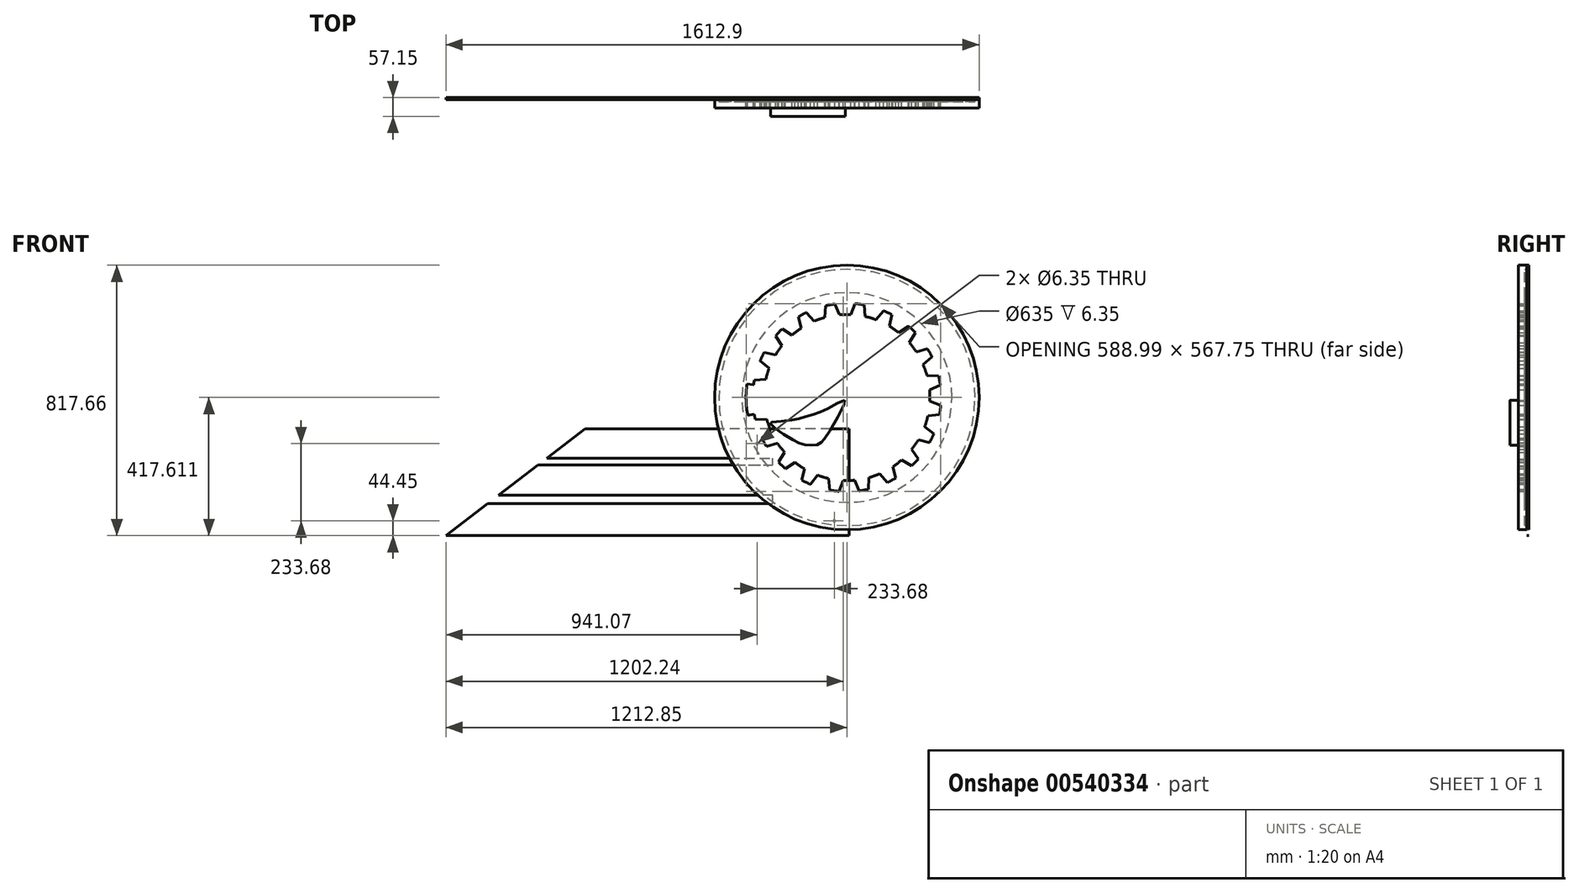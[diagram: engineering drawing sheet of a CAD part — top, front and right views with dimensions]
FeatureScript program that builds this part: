
annotation { "Feature Type Name" : "Feature", "Feature Type Description" : "" }
export const myFeature = defineFeature(function(context is Context, id is Id, definition is map)
    precondition{}
    {
        {
            var Q0;
            Q0=qCreatedBy(makeId("Front.planeOp"),FACE);
            var sketch = newSketch(context, id + "F0", { "sketchPlane" : qUnion([Q0])});
            skLineSegment(sketch, "E0", {"start": v(0, -90.2) * mm, "end": v(0, 1030.2) * mm, "construction": true});
            skLineSegment(sketch, "E1", {"start": v(0, 0) * mm, "end": v(-1219.2, 0) * mm});
            skLineSegment(sketch, "E2", {"start": v(-1219.2, 0) * mm, "end": v(-610.08, 467.36) * mm, "construction": true});
            skLineSegment(sketch, "E3", {"start": v(-1219.2, 0) * mm, "end": v(-1093.4, 96.52) * mm});
            skLineSegment(sketch, "E4", {"start": v(-1093.4, 96.52) * mm, "end": v(-231.3, 96.52) * mm});
            skLineSegment(sketch, "E5", {"start": v(0, 96.52) * mm, "end": v(0, 0) * mm});
            skLineSegment(sketch, "E6", {"start": v(-231.3, 121.92) * mm, "end": v(-1060.3, 121.92) * mm});
            skLineSegment(sketch, "E7", {"start": v(-1060.3, 121.92) * mm, "end": v(-941.12, 213.36) * mm});
            skLineSegment(sketch, "E8", {"start": v(-941.12, 213.36) * mm, "end": v(-231.3, 213.36) * mm});
            skLineSegment(sketch, "E9", {"start": v(0, 213.36) * mm, "end": v(0, 121.92) * mm});
            skLineSegment(sketch, "E10", {"start": v(-914.64, 233.68) * mm, "end": v(-231.3, 233.68) * mm});
            skLineSegment(sketch, "E11", {"start": v(0, 233.68) * mm, "end": v(0, 322.58) * mm});
            skLineSegment(sketch, "E12", {"start": v(0, 322.58) * mm, "end": v(-798.77, 322.58) * mm});
            skLineSegment(sketch, "E13", {"start": v(-798.77, 322.58) * mm, "end": v(-914.64, 233.68) * mm});
            skLineSegment(sketch, "E14", {"start": v(-231.3, 96.52) * mm, "end": v(-231.3, 121.92) * mm});
            skLineSegment(sketch, "E15", {"start": v(-231.3, 322.58) * mm, "end": v(0, 322.58) * mm});
            skLineSegment(sketch, "E16.trimOffspring", {"start": v(-231.3, 213.36) * mm, "end": v(-231.3, 233.68) * mm});
            skLineSegment(sketch, "E17", {"start": v(0, 322.58) * mm, "end": v(0, 0) * mm});
            skLineSegment(sketch, "E18", {"start": v(-322.58, 322.58) * mm, "end": v(-322.58, 0) * mm, "construction": true});
            skLineSegment(sketch, "E19", {"start": v(-322.58, 322.58) * mm, "end": v(0, 0) * mm, "construction": true});
            skLineSegment(sketch, "E20", {"start": v(0, 278.13) * mm, "end": v(-322.58, 278.13) * mm, "construction": true});
            skPoint(sketch, "E21.start.orphan", {"position": v(0, 48.26) * mm});
            skLineSegment(sketch, "E22.0", {"start": v(0, 44.45) * mm, "end": v(-1219.2, 44.45) * mm, "construction": true});
            skCircle(sketch, "E23", {"center": v(-278.13, 278.13) * mm, "radius": 3.18 * mm});
            skCircle(sketch, "E24", {"center": v(-44.45, 44.45) * mm, "radius": 3.18 * mm});
            skSolve(sketch);
        }
        {
            var Q0;
            {var subQ0=sQuery(id+"F0.wireOp",EDGE,"E1");Q0=makeQuery(id+"F0.imprint","IMPRINT",FACE,{"disambiguationData":[TD([[makeQuery(id+"F0.imprint","IMPRINT",EDGE,{"derivedFrom":subQ0}),-1.0]])]});}
            extrude(context, id + "F1", {"entities" : qUnion([Q0]), "depth" : 6.35 * mm, "offsetDistance" : 25.4 * mm});
        }
        {
            var Q0;
            Q0=qCreatedBy(makeId("Front.planeOp"),FACE);
            var sketch = newSketch(context, id + "F2", { "sketchPlane" : qUnion([Q0])});
            skCircle(sketch, "E25", {"center": v(-6.35, 417.61) * mm, "radius": 400.05 * mm});
            skSolve(sketch);
        }
        {
            var Q0;
            Q0 = qSketchRegion(id + "F2", true);
            extrude(context, id + "F3", {"entities" : qUnion([Q0]), "depth" : 6.35 * mm, "offsetDistance" : 25.4 * mm});
        }
        {
            var Q0;
            Q0=makeQuery(id+"F3.opExtrude","CAP_FACE",FACE,{"disambiguationData":[OSD([sQuery(id+"F2.wireOp",EDGE,"E25")])],"isStart":false});
            var sketch = newSketch(context, id + "F4", { "sketchPlane" : qUnion([Q0])});
            skCircle(sketch, "E26.0", {"center": v(-6.35, 417.61) * mm, "radius": 400.05 * mm});
            skCircle(sketch, "E27", {"center": v(-6.35, 417.61) * mm, "radius": 387.35 * mm});
            skCircle(sketch, "E28", {"center": v(-6.35, 417.61) * mm, "radius": 317.5 * mm});
            skSolve(sketch);
        }
        {
            var Q0;
            Q0=makeQuery(id+"F4.imprint","IMPRINT",FACE,{"disambiguationData":[TD([[makeQuery(id+"F4.imprint","IMPRINT",EDGE,{"derivedFrom":sQuery(id+"F4.wireOp",EDGE,"E27")}),1.0]])]});
            extrude(context, id + "F5", {"entities" : qUnion([Q0]), "depth" : 6.35 * mm, "offsetDistance" : 25.4 * mm});
        }
        {
            var Q0;
            Q0=makeQuery(id+"F3.opExtrude","CAP_FACE",FACE,{"disambiguationData":[OSD([sQuery(id+"F2.wireOp",EDGE,"E25")])],"isStart":false});
            var sketch = newSketch(context, id + "F6", { "sketchPlane" : qUnion([Q0])});
            skCircle(sketch, "E29.0", {"center": v(-6.35, 417.61) * mm, "radius": 400.05 * mm});
            skArc(sketch, "E30", {"start": v(-306.57, 363) * mm, "mid": v(-309.93, 386.72) * mm, "end": v(-311.42, 410.64) * mm});
            skArc(sketch, "E31", {"start": v(-286.62, 366.63) * mm, "mid": v(-287.82, 373.7) * mm, "end": v(-288.84, 380.81) * mm});
            skArc(sketch, "E32", {"start": v(-256.45, 394.63) * mm, "mid": v(-257.1, 403.24) * mm, "end": v(-257.44, 411.87) * mm});
            skLineSegment(sketch, "E33", {"start": v(-306.57, 363) * mm, "end": v(-286.62, 366.63) * mm});
            skLineSegment(sketch, "E34", {"start": v(-288.84, 380.81) * mm, "end": v(-256.45, 394.63) * mm});
            skArc(sketch, "E35.MirrorCS", {"start": v(-257.24, 429.14) * mm, "mid": v(-257.5, 420.5) * mm, "end": v(-257.44, 411.87) * mm});
            skLineSegment(sketch, "E36.MirrorCS", {"start": v(-290.22, 441.47) * mm, "end": v(-257.24, 429.14) * mm});
            skArc(sketch, "E37.MirrorCS", {"start": v(-288.66, 455.73) * mm, "mid": v(-289.53, 448.6) * mm, "end": v(-290.22, 441.47) * mm});
            skArc(sketch, "E38.MirrorCS", {"start": v(-308.75, 458.45) * mm, "mid": v(-311.02, 434.6) * mm, "end": v(-311.42, 410.64) * mm});
            skPoint(sketch, "E39.orphan", {"position": v(-402.8, 471.15) * mm});
            skLineSegment(sketch, "E40.trimOffspring", {"start": v(-406.3, 408.47) * mm, "end": v(-408.84, 408.41) * mm, "construction": true});
            skArc(sketch, "E41.1.0", {"start": v(-306.57, 363) * mm, "mid": v(-301.36, 339.61) * mm, "end": v(-294.33, 316.7) * mm});
            skLineSegment(sketch, "E41.1.1", {"start": v(-257.15, 282.51) * mm, "end": v(-275, 272.9) * mm, "construction": true});
            skLineSegment(sketch, "E41.1.2", {"start": v(-263.64, 295.32) * mm, "end": v(-237.1, 318.46) * mm});
            skArc(sketch, "E41.1.3", {"start": v(-286.62, 366.63) * mm, "mid": v(-285.25, 359.58) * mm, "end": v(-283.7, 352.57) * mm});
            skArc(sketch, "E41.1.5", {"start": v(-248.53, 351.05) * mm, "mid": v(-246.1, 342.76) * mm, "end": v(-243.38, 334.56) * mm});
            skLineSegment(sketch, "E41.1.6", {"start": v(-283.7, 352.57) * mm, "end": v(-248.53, 351.05) * mm});
            skArc(sketch, "E41.1.7", {"start": v(-257.15, 282.51) * mm, "mid": v(-260.48, 288.87) * mm, "end": v(-263.64, 295.32) * mm});
            skArc(sketch, "E41.1.8", {"start": v(-275, 272.9) * mm, "mid": v(-285.53, 294.42) * mm, "end": v(-294.33, 316.7) * mm});
            skArc(sketch, "E41.1.9", {"start": v(-237.1, 318.46) * mm, "mid": v(-240.38, 326.46) * mm, "end": v(-243.38, 334.56) * mm});
            skArc(sketch, "E41.1.10", {"start": v(-306.57, 363) * mm, "mid": v(-301.36, 339.61) * mm, "end": v(-294.33, 316.7) * mm});
            skLineSegment(sketch, "E41.1.11", {"start": v(-275, 272.9) * mm, "end": v(-257.15, 282.51) * mm});
            skArc(sketch, "E41.1.12", {"start": v(-286.62, 366.63) * mm, "mid": v(-285.25, 359.58) * mm, "end": v(-283.7, 352.57) * mm});
            skArc(sketch, "E41.2.0", {"start": v(-275, 272.9) * mm, "mid": v(-262.82, 252.27) * mm, "end": v(-249.05, 232.65) * mm});
            skLineSegment(sketch, "E41.2.1", {"start": v(-203.13, 211.62) * mm, "end": v(-217.13, 196.96) * mm, "construction": true});
            skLineSegment(sketch, "E41.2.2", {"start": v(-213.26, 221.8) * mm, "end": v(-195.18, 252) * mm});
            skArc(sketch, "E41.2.3", {"start": v(-257.15, 282.51) * mm, "mid": v(-253.67, 276.24) * mm, "end": v(-250.03, 270.05) * mm});
            skLineSegment(sketch, "E41.2.4", {"start": v(-257.15, 282.51) * mm, "end": v(-275, 272.9) * mm, "construction": true});
            skArc(sketch, "E41.2.5", {"start": v(-216.1, 279.47) * mm, "mid": v(-211.23, 272.34) * mm, "end": v(-206.11, 265.38) * mm});
            skLineSegment(sketch, "E41.2.6", {"start": v(-250.03, 270.05) * mm, "end": v(-216.1, 279.47) * mm});
            skArc(sketch, "E41.2.7", {"start": v(-203.13, 211.62) * mm, "mid": v(-208.26, 216.64) * mm, "end": v(-213.26, 221.8) * mm});
            skArc(sketch, "E41.2.8", {"start": v(-217.13, 196.96) * mm, "mid": v(-233.8, 214.18) * mm, "end": v(-249.05, 232.65) * mm});
            skArc(sketch, "E41.2.9", {"start": v(-195.18, 252) * mm, "mid": v(-200.76, 258.6) * mm, "end": v(-206.11, 265.38) * mm});
            skArc(sketch, "E41.2.10", {"start": v(-275, 272.9) * mm, "mid": v(-262.82, 252.27) * mm, "end": v(-249.05, 232.65) * mm});
            skLineSegment(sketch, "E41.2.11", {"start": v(-217.13, 196.96) * mm, "end": v(-203.13, 211.62) * mm});
            skArc(sketch, "E41.2.12", {"start": v(-257.15, 282.51) * mm, "mid": v(-253.67, 276.24) * mm, "end": v(-250.03, 270.05) * mm});
            skLineSegment(sketch, "E41.2.13", {"start": v(-275, 272.9) * mm, "end": v(-257.15, 282.51) * mm});
            skArc(sketch, "E41.3.0", {"start": v(-217.13, 196.96) * mm, "mid": v(-199.17, 181.1) * mm, "end": v(-180.02, 166.7) * mm});
            skLineSegment(sketch, "E41.3.1", {"start": v(-129.84, 160.9) * mm, "end": v(-138.63, 142.63) * mm, "construction": true});
            skLineSegment(sketch, "E41.3.2", {"start": v(-142.62, 167.44) * mm, "end": v(-134.76, 201.76) * mm});
            skArc(sketch, "E41.3.3", {"start": v(-203.13, 211.62) * mm, "mid": v(-197.88, 206.73) * mm, "end": v(-192.5, 201.97) * mm});
            skLineSegment(sketch, "E41.3.4", {"start": v(-203.13, 211.62) * mm, "end": v(-217.13, 196.96) * mm, "construction": true});
            skArc(sketch, "E41.3.5", {"start": v(-163.15, 221.41) * mm, "mid": v(-156.3, 216.13) * mm, "end": v(-149.3, 211.1) * mm});
            skLineSegment(sketch, "E41.3.6", {"start": v(-192.5, 201.97) * mm, "end": v(-163.15, 221.41) * mm});
            skArc(sketch, "E41.3.7", {"start": v(-129.84, 160.9) * mm, "mid": v(-136.27, 164.09) * mm, "end": v(-142.62, 167.44) * mm});
            skArc(sketch, "E41.3.8", {"start": v(-138.63, 142.63) * mm, "mid": v(-159.8, 153.85) * mm, "end": v(-180.02, 166.7) * mm});
            skArc(sketch, "E41.3.9", {"start": v(-134.76, 201.76) * mm, "mid": v(-142.1, 206.3) * mm, "end": v(-149.3, 211.1) * mm});
            skArc(sketch, "E41.3.10", {"start": v(-217.13, 196.96) * mm, "mid": v(-199.17, 181.1) * mm, "end": v(-180.02, 166.7) * mm});
            skLineSegment(sketch, "E41.3.11", {"start": v(-138.63, 142.63) * mm, "end": v(-129.84, 160.9) * mm});
            skArc(sketch, "E41.3.12", {"start": v(-203.13, 211.62) * mm, "mid": v(-197.88, 206.73) * mm, "end": v(-192.5, 201.97) * mm});
            skLineSegment(sketch, "E41.3.13", {"start": v(-217.13, 196.96) * mm, "end": v(-203.13, 211.62) * mm});
            skArc(sketch, "E41.4.0", {"start": v(-138.63, 142.63) * mm, "mid": v(-116.65, 133.1) * mm, "end": v(-93.99, 125.32) * mm});
            skLineSegment(sketch, "E41.4.1", {"start": v(-44.47, 135.3) * mm, "end": v(-47.18, 115.2) * mm, "construction": true});
            skLineSegment(sketch, "E41.4.2", {"start": v(-58.64, 137.57) * mm, "end": v(-61.77, 172.64) * mm});
            skArc(sketch, "E41.4.3", {"start": v(-129.84, 160.9) * mm, "mid": v(-123.34, 157.86) * mm, "end": v(-116.76, 155) * mm});
            skLineSegment(sketch, "E41.4.4", {"start": v(-129.84, 160.9) * mm, "end": v(-138.63, 142.63) * mm, "construction": true});
            skArc(sketch, "E41.4.5", {"start": v(-94.85, 182.56) * mm, "mid": v(-86.71, 179.65) * mm, "end": v(-78.48, 177.03) * mm});
            skLineSegment(sketch, "E41.4.6", {"start": v(-116.76, 155) * mm, "end": v(-94.85, 182.56) * mm});
            skArc(sketch, "E41.4.7", {"start": v(-44.47, 135.3) * mm, "mid": v(-51.57, 136.35) * mm, "end": v(-58.64, 137.57) * mm});
            skArc(sketch, "E41.4.8", {"start": v(-47.18, 115.2) * mm, "mid": v(-70.78, 119.34) * mm, "end": v(-93.99, 125.32) * mm});
            skArc(sketch, "E41.4.9", {"start": v(-61.77, 172.64) * mm, "mid": v(-70.16, 174.7) * mm, "end": v(-78.48, 177.03) * mm});
            skArc(sketch, "E41.4.10", {"start": v(-138.63, 142.63) * mm, "mid": v(-116.65, 133.1) * mm, "end": v(-93.99, 125.32) * mm});
            skLineSegment(sketch, "E41.4.11", {"start": v(-47.18, 115.2) * mm, "end": v(-44.47, 135.3) * mm});
            skArc(sketch, "E41.4.12", {"start": v(-129.84, 160.9) * mm, "mid": v(-123.34, 157.86) * mm, "end": v(-116.76, 155) * mm});
            skLineSegment(sketch, "E41.4.13", {"start": v(-138.63, 142.63) * mm, "end": v(-129.84, 160.9) * mm});
            skArc(sketch, "E41.5.0", {"start": v(-47.18, 115.2) * mm, "mid": v(-23.33, 112.93) * mm, "end": v(0.63, 112.54) * mm});
            skLineSegment(sketch, "E41.5.1", {"start": v(44.64, 137.33) * mm, "end": v(48.26, 117.39) * mm, "construction": true});
            skLineSegment(sketch, "E41.5.2", {"start": v(30.45, 135.12) * mm, "end": v(16.64, 167.5) * mm});
            skArc(sketch, "E41.5.3", {"start": v(-44.47, 135.3) * mm, "mid": v(-37.34, 134.43) * mm, "end": v(-30.2, 133.73) * mm});
            skLineSegment(sketch, "E41.5.4", {"start": v(-44.47, 135.3) * mm, "end": v(-47.18, 115.2) * mm, "construction": true});
            skArc(sketch, "E41.5.5", {"start": v(-17.88, 166.72) * mm, "mid": v(-9.24, 166.47) * mm, "end": v(-0.6, 166.52) * mm});
            skLineSegment(sketch, "E41.5.6", {"start": v(-30.2, 133.73) * mm, "end": v(-17.88, 166.72) * mm});
            skArc(sketch, "E41.5.7", {"start": v(44.64, 137.33) * mm, "mid": v(37.56, 136.14) * mm, "end": v(30.45, 135.12) * mm});
            skArc(sketch, "E41.5.8", {"start": v(48.26, 117.39) * mm, "mid": v(24.54, 114.03) * mm, "end": v(0.63, 112.54) * mm});
            skArc(sketch, "E41.5.9", {"start": v(16.64, 167.5) * mm, "mid": v(8.02, 166.86) * mm, "end": v(-0.6, 166.52) * mm});
            skArc(sketch, "E41.5.10", {"start": v(-47.18, 115.2) * mm, "mid": v(-23.33, 112.93) * mm, "end": v(0.63, 112.54) * mm});
            skLineSegment(sketch, "E41.5.11", {"start": v(48.26, 117.39) * mm, "end": v(44.64, 137.33) * mm});
            skArc(sketch, "E41.5.12", {"start": v(-44.47, 135.3) * mm, "mid": v(-37.34, 134.43) * mm, "end": v(-30.2, 133.73) * mm});
            skLineSegment(sketch, "E41.5.13", {"start": v(-47.18, 115.2) * mm, "end": v(-44.47, 135.3) * mm});
            skArc(sketch, "E41.6.0", {"start": v(48.26, 117.39) * mm, "mid": v(71.65, 122.6) * mm, "end": v(94.56, 129.63) * mm});
            skLineSegment(sketch, "E41.6.1", {"start": v(128.75, 166.8) * mm, "end": v(138.37, 148.96) * mm, "construction": true});
            skLineSegment(sketch, "E41.6.2", {"start": v(115.95, 160.32) * mm, "end": v(92.8, 186.85) * mm});
            skArc(sketch, "E41.6.3", {"start": v(44.64, 137.33) * mm, "mid": v(51.68, 138.7) * mm, "end": v(58.7, 140.26) * mm});
            skLineSegment(sketch, "E41.6.4", {"start": v(44.64, 137.33) * mm, "end": v(48.26, 117.39) * mm, "construction": true});
            skArc(sketch, "E41.6.5", {"start": v(60.22, 175.43) * mm, "mid": v(68.5, 177.86) * mm, "end": v(76.7, 180.58) * mm});
            skLineSegment(sketch, "E41.6.6", {"start": v(58.7, 140.26) * mm, "end": v(60.22, 175.43) * mm});
            skArc(sketch, "E41.6.7", {"start": v(128.75, 166.8) * mm, "mid": v(122.4, 163.48) * mm, "end": v(115.95, 160.32) * mm});
            skArc(sketch, "E41.6.8", {"start": v(138.37, 148.96) * mm, "mid": v(116.84, 138.43) * mm, "end": v(94.56, 129.63) * mm});
            skArc(sketch, "E41.6.9", {"start": v(92.8, 186.85) * mm, "mid": v(84.8, 183.57) * mm, "end": v(76.7, 180.58) * mm});
            skArc(sketch, "E41.6.10", {"start": v(48.26, 117.39) * mm, "mid": v(71.65, 122.6) * mm, "end": v(94.56, 129.63) * mm});
            skLineSegment(sketch, "E41.6.11", {"start": v(138.37, 148.96) * mm, "end": v(128.75, 166.8) * mm});
            skArc(sketch, "E41.6.12", {"start": v(44.64, 137.33) * mm, "mid": v(51.68, 138.7) * mm, "end": v(58.7, 140.26) * mm});
            skLineSegment(sketch, "E41.6.13", {"start": v(48.26, 117.39) * mm, "end": v(44.64, 137.33) * mm});
            skArc(sketch, "E41.7.0", {"start": v(138.37, 148.96) * mm, "mid": v(159, 161.14) * mm, "end": v(178.61, 174.9) * mm});
            skLineSegment(sketch, "E41.7.1", {"start": v(199.64, 220.83) * mm, "end": v(214.3, 206.83) * mm, "construction": true});
            skLineSegment(sketch, "E41.7.2", {"start": v(189.47, 210.7) * mm, "end": v(159.26, 228.78) * mm});
            skArc(sketch, "E41.7.3", {"start": v(128.75, 166.8) * mm, "mid": v(135.03, 170.29) * mm, "end": v(141.21, 173.93) * mm});
            skLineSegment(sketch, "E41.7.4", {"start": v(128.75, 166.8) * mm, "end": v(138.37, 148.96) * mm, "construction": true});
            skArc(sketch, "E41.7.5", {"start": v(131.8, 207.85) * mm, "mid": v(138.93, 212.73) * mm, "end": v(145.89, 217.84) * mm});
            skLineSegment(sketch, "E41.7.6", {"start": v(141.21, 173.93) * mm, "end": v(131.8, 207.85) * mm});
            skArc(sketch, "E41.7.7", {"start": v(199.64, 220.83) * mm, "mid": v(194.62, 215.7) * mm, "end": v(189.47, 210.7) * mm});
            skArc(sketch, "E41.7.8", {"start": v(214.3, 206.83) * mm, "mid": v(197.08, 190.16) * mm, "end": v(178.61, 174.9) * mm});
            skArc(sketch, "E41.7.9", {"start": v(159.26, 228.78) * mm, "mid": v(152.67, 223.2) * mm, "end": v(145.89, 217.84) * mm});
            skArc(sketch, "E41.7.10", {"start": v(138.37, 148.96) * mm, "mid": v(159, 161.14) * mm, "end": v(178.61, 174.9) * mm});
            skLineSegment(sketch, "E41.7.11", {"start": v(214.3, 206.83) * mm, "end": v(199.64, 220.83) * mm});
            skArc(sketch, "E41.7.12", {"start": v(128.75, 166.8) * mm, "mid": v(135.03, 170.29) * mm, "end": v(141.21, 173.93) * mm});
            skLineSegment(sketch, "E41.7.13", {"start": v(138.37, 148.96) * mm, "end": v(128.75, 166.8) * mm});
            skArc(sketch, "E41.8.0", {"start": v(214.3, 206.83) * mm, "mid": v(230.16, 224.79) * mm, "end": v(244.56, 243.94) * mm});
            skLineSegment(sketch, "E41.8.1", {"start": v(250.37, 294.11) * mm, "end": v(268.64, 285.33) * mm, "construction": true});
            skLineSegment(sketch, "E41.8.2", {"start": v(243.82, 281.34) * mm, "end": v(209.5, 289.2) * mm});
            skArc(sketch, "E41.8.3", {"start": v(199.64, 220.83) * mm, "mid": v(204.54, 226.08) * mm, "end": v(209.3, 231.45) * mm});
            skLineSegment(sketch, "E41.8.4", {"start": v(199.64, 220.83) * mm, "end": v(214.3, 206.83) * mm, "construction": true});
            skArc(sketch, "E41.8.5", {"start": v(189.85, 260.8) * mm, "mid": v(195.13, 267.65) * mm, "end": v(200.17, 274.66) * mm});
            skLineSegment(sketch, "E41.8.6", {"start": v(209.3, 231.45) * mm, "end": v(189.85, 260.8) * mm});
            skArc(sketch, "E41.8.7", {"start": v(250.37, 294.11) * mm, "mid": v(247.18, 287.69) * mm, "end": v(243.82, 281.34) * mm});
            skArc(sketch, "E41.8.8", {"start": v(268.64, 285.33) * mm, "mid": v(257.41, 264.16) * mm, "end": v(244.56, 243.94) * mm});
            skArc(sketch, "E41.8.9", {"start": v(209.5, 289.2) * mm, "mid": v(204.96, 281.85) * mm, "end": v(200.17, 274.66) * mm});
            skArc(sketch, "E41.8.10", {"start": v(214.3, 206.83) * mm, "mid": v(230.16, 224.79) * mm, "end": v(244.56, 243.94) * mm});
            skLineSegment(sketch, "E41.8.11", {"start": v(268.64, 285.33) * mm, "end": v(250.37, 294.11) * mm});
            skArc(sketch, "E41.8.12", {"start": v(199.64, 220.83) * mm, "mid": v(204.54, 226.08) * mm, "end": v(209.3, 231.45) * mm});
            skLineSegment(sketch, "E41.8.13", {"start": v(214.3, 206.83) * mm, "end": v(199.64, 220.83) * mm});
            skArc(sketch, "E41.9.0", {"start": v(268.64, 285.33) * mm, "mid": v(278.17, 307.3) * mm, "end": v(285.95, 329.97) * mm});
            skLineSegment(sketch, "E41.9.1", {"start": v(275.97, 379.49) * mm, "end": v(296.06, 376.78) * mm, "construction": true});
            skLineSegment(sketch, "E41.9.2", {"start": v(273.7, 365.32) * mm, "end": v(238.62, 362.18) * mm});
            skArc(sketch, "E41.9.3", {"start": v(250.37, 294.11) * mm, "mid": v(253.4, 300.62) * mm, "end": v(256.27, 307.2) * mm});
            skLineSegment(sketch, "E41.9.4", {"start": v(250.37, 294.11) * mm, "end": v(268.64, 285.33) * mm, "construction": true});
            skArc(sketch, "E41.9.5", {"start": v(228.7, 329.11) * mm, "mid": v(231.61, 337.25) * mm, "end": v(234.23, 345.48) * mm});
            skLineSegment(sketch, "E41.9.6", {"start": v(256.27, 307.2) * mm, "end": v(228.7, 329.11) * mm});
            skArc(sketch, "E41.9.7", {"start": v(275.97, 379.49) * mm, "mid": v(274.92, 372.39) * mm, "end": v(273.7, 365.32) * mm});
            skArc(sketch, "E41.9.8", {"start": v(296.06, 376.78) * mm, "mid": v(291.92, 353.17) * mm, "end": v(285.95, 329.97) * mm});
            skArc(sketch, "E41.9.9", {"start": v(238.62, 362.18) * mm, "mid": v(236.57, 353.8) * mm, "end": v(234.23, 345.48) * mm});
            skArc(sketch, "E41.9.10", {"start": v(268.64, 285.33) * mm, "mid": v(278.17, 307.3) * mm, "end": v(285.95, 329.97) * mm});
            skLineSegment(sketch, "E41.9.11", {"start": v(296.06, 376.78) * mm, "end": v(275.97, 379.49) * mm});
            skArc(sketch, "E41.9.12", {"start": v(250.37, 294.11) * mm, "mid": v(253.4, 300.62) * mm, "end": v(256.27, 307.2) * mm});
            skLineSegment(sketch, "E41.9.13", {"start": v(268.64, 285.33) * mm, "end": v(250.37, 294.11) * mm});
            skArc(sketch, "E41.10.0", {"start": v(296.06, 376.78) * mm, "mid": v(298.33, 400.63) * mm, "end": v(298.72, 424.58) * mm});
            skLineSegment(sketch, "E41.10.1", {"start": v(273.93, 468.6) * mm, "end": v(293.88, 472.22) * mm, "construction": true});
            skLineSegment(sketch, "E41.10.2", {"start": v(276.15, 454.41) * mm, "end": v(243.76, 440.6) * mm});
            skArc(sketch, "E41.10.3", {"start": v(275.97, 379.49) * mm, "mid": v(276.84, 386.61) * mm, "end": v(277.53, 393.76) * mm});
            skLineSegment(sketch, "E41.10.4", {"start": v(275.97, 379.49) * mm, "end": v(296.06, 376.78) * mm, "construction": true});
            skArc(sketch, "E41.10.5", {"start": v(244.55, 406.08) * mm, "mid": v(244.8, 414.71) * mm, "end": v(244.75, 423.35) * mm});
            skLineSegment(sketch, "E41.10.6", {"start": v(277.53, 393.76) * mm, "end": v(244.55, 406.08) * mm});
            skArc(sketch, "E41.10.7", {"start": v(273.93, 468.6) * mm, "mid": v(275.13, 461.52) * mm, "end": v(276.15, 454.41) * mm});
            skArc(sketch, "E41.10.8", {"start": v(293.88, 472.22) * mm, "mid": v(297.24, 448.5) * mm, "end": v(298.72, 424.58) * mm});
            skArc(sketch, "E41.10.9", {"start": v(243.76, 440.6) * mm, "mid": v(244.4, 431.98) * mm, "end": v(244.75, 423.35) * mm});
            skArc(sketch, "E41.10.10", {"start": v(296.06, 376.78) * mm, "mid": v(298.33, 400.63) * mm, "end": v(298.72, 424.58) * mm});
            skLineSegment(sketch, "E41.10.11", {"start": v(293.88, 472.22) * mm, "end": v(273.93, 468.6) * mm});
            skArc(sketch, "E41.10.12", {"start": v(275.97, 379.49) * mm, "mid": v(276.84, 386.61) * mm, "end": v(277.53, 393.76) * mm});
            skLineSegment(sketch, "E41.10.13", {"start": v(296.06, 376.78) * mm, "end": v(275.97, 379.49) * mm});
            skArc(sketch, "E41.11.0", {"start": v(293.88, 472.22) * mm, "mid": v(288.67, 495.6) * mm, "end": v(281.64, 518.52) * mm});
            skLineSegment(sketch, "E41.11.1", {"start": v(244.46, 552.7) * mm, "end": v(262.3, 562.32) * mm, "construction": true});
            skLineSegment(sketch, "E41.11.2", {"start": v(250.95, 539.9) * mm, "end": v(224.42, 516.76) * mm});
            skArc(sketch, "E41.11.3", {"start": v(273.93, 468.6) * mm, "mid": v(272.56, 475.64) * mm, "end": v(271, 482.65) * mm});
            skLineSegment(sketch, "E41.11.4", {"start": v(273.93, 468.6) * mm, "end": v(293.88, 472.22) * mm, "construction": true});
            skArc(sketch, "E41.11.5", {"start": v(235.83, 484.17) * mm, "mid": v(233.4, 492.46) * mm, "end": v(230.69, 500.66) * mm});
            skLineSegment(sketch, "E41.11.6", {"start": v(271, 482.65) * mm, "end": v(235.83, 484.17) * mm});
            skArc(sketch, "E41.11.7", {"start": v(244.46, 552.7) * mm, "mid": v(247.78, 546.35) * mm, "end": v(250.95, 539.9) * mm});
            skArc(sketch, "E41.11.8", {"start": v(262.3, 562.32) * mm, "mid": v(272.83, 540.8) * mm, "end": v(281.64, 518.52) * mm});
            skArc(sketch, "E41.11.9", {"start": v(224.42, 516.76) * mm, "mid": v(227.7, 508.76) * mm, "end": v(230.69, 500.66) * mm});
            skArc(sketch, "E41.11.10", {"start": v(293.88, 472.22) * mm, "mid": v(288.67, 495.6) * mm, "end": v(281.64, 518.52) * mm});
            skLineSegment(sketch, "E41.11.11", {"start": v(262.3, 562.32) * mm, "end": v(244.46, 552.7) * mm});
            skArc(sketch, "E41.11.12", {"start": v(273.93, 468.6) * mm, "mid": v(272.56, 475.64) * mm, "end": v(271, 482.65) * mm});
            skLineSegment(sketch, "E41.11.13", {"start": v(293.88, 472.22) * mm, "end": v(273.93, 468.6) * mm});
            skArc(sketch, "E41.12.0", {"start": v(262.3, 562.32) * mm, "mid": v(250.13, 582.96) * mm, "end": v(236.36, 602.57) * mm});
            skLineSegment(sketch, "E41.12.1", {"start": v(190.44, 623.6) * mm, "end": v(204.44, 638.26) * mm, "construction": true});
            skLineSegment(sketch, "E41.12.2", {"start": v(200.56, 613.43) * mm, "end": v(182.48, 583.22) * mm});
            skArc(sketch, "E41.12.3", {"start": v(244.46, 552.7) * mm, "mid": v(240.98, 558.99) * mm, "end": v(237.34, 565.17) * mm});
            skLineSegment(sketch, "E41.12.4", {"start": v(244.46, 552.7) * mm, "end": v(262.3, 562.32) * mm, "construction": true});
            skArc(sketch, "E41.12.5", {"start": v(203.41, 555.75) * mm, "mid": v(198.54, 562.89) * mm, "end": v(193.42, 569.85) * mm});
            skLineSegment(sketch, "E41.12.6", {"start": v(237.34, 565.17) * mm, "end": v(203.41, 555.75) * mm});
            skArc(sketch, "E41.12.7", {"start": v(190.44, 623.6) * mm, "mid": v(195.56, 618.58) * mm, "end": v(200.56, 613.43) * mm});
            skArc(sketch, "E41.12.8", {"start": v(204.44, 638.26) * mm, "mid": v(221.1, 621.04) * mm, "end": v(236.36, 602.57) * mm});
            skArc(sketch, "E41.12.9", {"start": v(182.48, 583.22) * mm, "mid": v(188.07, 576.62) * mm, "end": v(193.42, 569.85) * mm});
            skArc(sketch, "E41.12.10", {"start": v(262.3, 562.32) * mm, "mid": v(250.13, 582.96) * mm, "end": v(236.36, 602.57) * mm});
            skLineSegment(sketch, "E41.12.11", {"start": v(204.44, 638.26) * mm, "end": v(190.44, 623.6) * mm});
            skArc(sketch, "E41.12.12", {"start": v(244.46, 552.7) * mm, "mid": v(240.98, 558.99) * mm, "end": v(237.34, 565.17) * mm});
            skLineSegment(sketch, "E41.12.13", {"start": v(262.3, 562.32) * mm, "end": v(244.46, 552.7) * mm});
            skArc(sketch, "E41.13.0", {"start": v(204.44, 638.26) * mm, "mid": v(186.48, 654.12) * mm, "end": v(167.33, 668.52) * mm});
            skLineSegment(sketch, "E41.13.1", {"start": v(117.15, 674.33) * mm, "end": v(125.94, 692.6) * mm, "construction": true});
            skLineSegment(sketch, "E41.13.2", {"start": v(129.93, 667.78) * mm, "end": v(122.07, 633.46) * mm});
            skArc(sketch, "E41.13.3", {"start": v(190.44, 623.6) * mm, "mid": v(185.18, 628.5) * mm, "end": v(179.81, 633.25) * mm});
            skLineSegment(sketch, "E41.13.4", {"start": v(190.44, 623.6) * mm, "end": v(204.44, 638.26) * mm, "construction": true});
            skArc(sketch, "E41.13.5", {"start": v(150.46, 613.81) * mm, "mid": v(143.62, 619.09) * mm, "end": v(136.6, 624.13) * mm});
            skLineSegment(sketch, "E41.13.6", {"start": v(179.81, 633.25) * mm, "end": v(150.46, 613.81) * mm});
            skArc(sketch, "E41.13.7", {"start": v(117.15, 674.33) * mm, "mid": v(123.58, 671.14) * mm, "end": v(129.93, 667.78) * mm});
            skArc(sketch, "E41.13.8", {"start": v(125.94, 692.6) * mm, "mid": v(147.1, 681.37) * mm, "end": v(167.33, 668.52) * mm});
            skArc(sketch, "E41.13.9", {"start": v(122.07, 633.46) * mm, "mid": v(129.41, 628.92) * mm, "end": v(136.6, 624.13) * mm});
            skArc(sketch, "E41.13.10", {"start": v(204.44, 638.26) * mm, "mid": v(186.48, 654.12) * mm, "end": v(167.33, 668.52) * mm});
            skLineSegment(sketch, "E41.13.11", {"start": v(125.94, 692.6) * mm, "end": v(117.15, 674.33) * mm});
            skArc(sketch, "E41.13.12", {"start": v(190.44, 623.6) * mm, "mid": v(185.18, 628.5) * mm, "end": v(179.81, 633.25) * mm});
            skLineSegment(sketch, "E41.13.13", {"start": v(204.44, 638.26) * mm, "end": v(190.44, 623.6) * mm});
            skArc(sketch, "E41.14.0", {"start": v(125.94, 692.6) * mm, "mid": v(103.96, 702.13) * mm, "end": v(81.3, 709.9) * mm});
            skLineSegment(sketch, "E41.14.1", {"start": v(31.78, 699.93) * mm, "end": v(34.5, 720.02) * mm, "construction": true});
            skLineSegment(sketch, "E41.14.2", {"start": v(45.95, 697.65) * mm, "end": v(49.08, 662.58) * mm});
            skArc(sketch, "E41.14.3", {"start": v(117.15, 674.33) * mm, "mid": v(110.64, 677.36) * mm, "end": v(104.06, 680.22) * mm});
            skLineSegment(sketch, "E41.14.4", {"start": v(117.15, 674.33) * mm, "end": v(125.94, 692.6) * mm, "construction": true});
            skArc(sketch, "E41.14.5", {"start": v(82.15, 652.66) * mm, "mid": v(74.02, 655.57) * mm, "end": v(65.79, 658.2) * mm});
            skLineSegment(sketch, "E41.14.6", {"start": v(104.06, 680.22) * mm, "end": v(82.15, 652.66) * mm});
            skArc(sketch, "E41.14.7", {"start": v(31.78, 699.93) * mm, "mid": v(38.88, 698.88) * mm, "end": v(45.95, 697.65) * mm});
            skArc(sketch, "E41.14.8", {"start": v(34.5, 720.02) * mm, "mid": v(58.1, 715.88) * mm, "end": v(81.3, 709.9) * mm});
            skArc(sketch, "E41.14.9", {"start": v(49.08, 662.58) * mm, "mid": v(57.47, 660.53) * mm, "end": v(65.79, 658.2) * mm});
            skArc(sketch, "E41.14.10", {"start": v(125.94, 692.6) * mm, "mid": v(103.96, 702.13) * mm, "end": v(81.3, 709.9) * mm});
            skLineSegment(sketch, "E41.14.11", {"start": v(34.5, 720.02) * mm, "end": v(31.78, 699.93) * mm});
            skArc(sketch, "E41.14.12", {"start": v(117.15, 674.33) * mm, "mid": v(110.64, 677.36) * mm, "end": v(104.06, 680.22) * mm});
            skLineSegment(sketch, "E41.14.13", {"start": v(125.94, 692.6) * mm, "end": v(117.15, 674.33) * mm});
            skArc(sketch, "E41.15.0", {"start": v(34.5, 720.02) * mm, "mid": v(10.64, 722.29) * mm, "end": v(-13.32, 722.68) * mm});
            skLineSegment(sketch, "E41.15.1", {"start": v(-57.33, 697.9) * mm, "end": v(-60.96, 717.83) * mm, "construction": true});
            skLineSegment(sketch, "E41.15.2", {"start": v(-43.15, 700.1) * mm, "end": v(-29.33, 667.72) * mm});
            skArc(sketch, "E41.15.3", {"start": v(31.78, 699.93) * mm, "mid": v(24.65, 700.8) * mm, "end": v(17.5, 701.49) * mm});
            skLineSegment(sketch, "E41.15.4", {"start": v(31.78, 699.93) * mm, "end": v(34.5, 720.02) * mm, "construction": true});
            skArc(sketch, "E41.15.5", {"start": v(5.19, 668.5) * mm, "mid": v(-3.45, 668.76) * mm, "end": v(-12.09, 668.7) * mm});
            skLineSegment(sketch, "E41.15.6", {"start": v(17.5, 701.49) * mm, "end": v(5.19, 668.5) * mm});
            skArc(sketch, "E41.15.7", {"start": v(-57.33, 697.9) * mm, "mid": v(-50.25, 699.09) * mm, "end": v(-43.15, 700.1) * mm});
            skArc(sketch, "E41.15.8", {"start": v(-60.96, 717.83) * mm, "mid": v(-37.23, 721.2) * mm, "end": v(-13.32, 722.68) * mm});
            skArc(sketch, "E41.15.9", {"start": v(-29.33, 667.72) * mm, "mid": v(-20.72, 668.36) * mm, "end": v(-12.09, 668.7) * mm});
            skArc(sketch, "E41.15.10", {"start": v(34.5, 720.02) * mm, "mid": v(10.64, 722.29) * mm, "end": v(-13.32, 722.68) * mm});
            skLineSegment(sketch, "E41.15.11", {"start": v(-60.96, 717.83) * mm, "end": v(-57.33, 697.9) * mm});
            skArc(sketch, "E41.15.12", {"start": v(31.78, 699.93) * mm, "mid": v(24.65, 700.8) * mm, "end": v(17.5, 701.49) * mm});
            skLineSegment(sketch, "E41.15.13", {"start": v(34.5, 720.02) * mm, "end": v(31.78, 699.93) * mm});
            skArc(sketch, "E41.16.0", {"start": v(-60.96, 717.83) * mm, "mid": v(-84.34, 712.62) * mm, "end": v(-107.25, 705.6) * mm});
            skLineSegment(sketch, "E41.16.1", {"start": v(-141.44, 668.42) * mm, "end": v(-151.06, 686.26) * mm, "construction": true});
            skLineSegment(sketch, "E41.16.2", {"start": v(-128.64, 674.9) * mm, "end": v(-105.5, 648.37) * mm});
            skArc(sketch, "E41.16.3", {"start": v(-57.33, 697.9) * mm, "mid": v(-64.37, 696.52) * mm, "end": v(-71.38, 694.97) * mm});
            skLineSegment(sketch, "E41.16.4", {"start": v(-57.33, 697.9) * mm, "end": v(-60.96, 717.83) * mm, "construction": true});
            skArc(sketch, "E41.16.5", {"start": v(-72.9, 659.8) * mm, "mid": v(-81.2, 657.36) * mm, "end": v(-89.4, 654.64) * mm});
            skLineSegment(sketch, "E41.16.6", {"start": v(-71.38, 694.97) * mm, "end": v(-72.9, 659.8) * mm});
            skArc(sketch, "E41.16.7", {"start": v(-141.44, 668.42) * mm, "mid": v(-135.08, 671.74) * mm, "end": v(-128.64, 674.9) * mm});
            skArc(sketch, "E41.16.8", {"start": v(-151.06, 686.26) * mm, "mid": v(-129.53, 696.8) * mm, "end": v(-107.25, 705.6) * mm});
            skArc(sketch, "E41.16.9", {"start": v(-105.5, 648.37) * mm, "mid": v(-97.5, 651.65) * mm, "end": v(-89.4, 654.64) * mm});
            skArc(sketch, "E41.16.10", {"start": v(-60.96, 717.83) * mm, "mid": v(-84.34, 712.62) * mm, "end": v(-107.25, 705.6) * mm});
            skLineSegment(sketch, "E41.16.11", {"start": v(-151.06, 686.26) * mm, "end": v(-141.44, 668.42) * mm});
            skArc(sketch, "E41.16.12", {"start": v(-57.33, 697.9) * mm, "mid": v(-64.37, 696.52) * mm, "end": v(-71.38, 694.97) * mm});
            skLineSegment(sketch, "E41.16.13", {"start": v(-60.96, 717.83) * mm, "end": v(-57.33, 697.9) * mm});
            skArc(sketch, "E41.17.0", {"start": v(-151.06, 686.26) * mm, "mid": v(-171.7, 674.08) * mm, "end": v(-191.3, 660.32) * mm});
            skLineSegment(sketch, "E41.17.1", {"start": v(-212.34, 614.4) * mm, "end": v(-227, 628.4) * mm, "construction": true});
            skLineSegment(sketch, "E41.17.2", {"start": v(-202.16, 624.52) * mm, "end": v(-171.95, 606.44) * mm});
            skArc(sketch, "E41.17.3", {"start": v(-141.44, 668.42) * mm, "mid": v(-147.72, 664.93) * mm, "end": v(-153.9, 661.3) * mm});
            skLineSegment(sketch, "E41.17.4", {"start": v(-141.44, 668.42) * mm, "end": v(-151.06, 686.26) * mm, "construction": true});
            skArc(sketch, "E41.17.5", {"start": v(-144.49, 627.37) * mm, "mid": v(-151.62, 622.5) * mm, "end": v(-158.58, 617.38) * mm});
            skLineSegment(sketch, "E41.17.6", {"start": v(-153.9, 661.3) * mm, "end": v(-144.49, 627.37) * mm});
            skArc(sketch, "E41.17.7", {"start": v(-212.34, 614.4) * mm, "mid": v(-207.31, 619.52) * mm, "end": v(-202.16, 624.52) * mm});
            skArc(sketch, "E41.17.8", {"start": v(-227, 628.4) * mm, "mid": v(-209.78, 645.06) * mm, "end": v(-191.3, 660.32) * mm});
            skArc(sketch, "E41.17.9", {"start": v(-171.95, 606.44) * mm, "mid": v(-165.36, 612.03) * mm, "end": v(-158.58, 617.38) * mm});
            skArc(sketch, "E41.17.10", {"start": v(-151.06, 686.26) * mm, "mid": v(-171.7, 674.08) * mm, "end": v(-191.3, 660.32) * mm});
            skLineSegment(sketch, "E41.17.11", {"start": v(-227, 628.4) * mm, "end": v(-212.34, 614.4) * mm});
            skArc(sketch, "E41.17.12", {"start": v(-141.44, 668.42) * mm, "mid": v(-147.72, 664.93) * mm, "end": v(-153.9, 661.3) * mm});
            skLineSegment(sketch, "E41.17.13", {"start": v(-151.06, 686.26) * mm, "end": v(-141.44, 668.42) * mm});
            skArc(sketch, "E41.18.0", {"start": v(-227, 628.4) * mm, "mid": v(-242.85, 610.44) * mm, "end": v(-257.25, 591.29) * mm});
            skLineSegment(sketch, "E41.18.1", {"start": v(-263.06, 541.1) * mm, "end": v(-281.33, 549.9) * mm, "construction": true});
            skLineSegment(sketch, "E41.18.2", {"start": v(-256.52, 553.88) * mm, "end": v(-222.2, 546.03) * mm});
            skArc(sketch, "E41.18.3", {"start": v(-212.34, 614.4) * mm, "mid": v(-217.23, 609.14) * mm, "end": v(-221.99, 603.77) * mm});
            skLineSegment(sketch, "E41.18.4", {"start": v(-212.34, 614.4) * mm, "end": v(-227, 628.4) * mm, "construction": true});
            skArc(sketch, "E41.18.5", {"start": v(-202.55, 574.41) * mm, "mid": v(-207.82, 567.58) * mm, "end": v(-212.86, 560.56) * mm});
            skLineSegment(sketch, "E41.18.6", {"start": v(-221.99, 603.77) * mm, "end": v(-202.55, 574.41) * mm});
            skArc(sketch, "E41.18.7", {"start": v(-263.06, 541.1) * mm, "mid": v(-259.87, 547.54) * mm, "end": v(-256.52, 553.88) * mm});
            skArc(sketch, "E41.18.8", {"start": v(-281.33, 549.9) * mm, "mid": v(-270.1, 571.06) * mm, "end": v(-257.25, 591.29) * mm});
            skArc(sketch, "E41.18.9", {"start": v(-222.2, 546.03) * mm, "mid": v(-217.65, 553.37) * mm, "end": v(-212.86, 560.56) * mm});
            skArc(sketch, "E41.18.10", {"start": v(-227, 628.4) * mm, "mid": v(-242.85, 610.44) * mm, "end": v(-257.25, 591.29) * mm});
            skLineSegment(sketch, "E41.18.11", {"start": v(-281.33, 549.9) * mm, "end": v(-263.06, 541.1) * mm});
            skArc(sketch, "E41.18.12", {"start": v(-212.34, 614.4) * mm, "mid": v(-217.23, 609.14) * mm, "end": v(-221.99, 603.77) * mm});
            skLineSegment(sketch, "E41.18.13", {"start": v(-227, 628.4) * mm, "end": v(-212.34, 614.4) * mm});
            skArc(sketch, "E41.19.0", {"start": v(-281.33, 549.9) * mm, "mid": v(-290.86, 527.91) * mm, "end": v(-298.64, 505.25) * mm});
            skLineSegment(sketch, "E41.19.2", {"start": v(-286.38, 469.9) * mm, "end": v(-251.31, 473.04) * mm});
            skArc(sketch, "E41.19.3", {"start": v(-263.06, 541.1) * mm, "mid": v(-266.1, 534.6) * mm, "end": v(-268.96, 528.02) * mm});
            skLineSegment(sketch, "E41.19.4", {"start": v(-263.06, 541.1) * mm, "end": v(-281.33, 549.9) * mm, "construction": true});
            skArc(sketch, "E41.19.5", {"start": v(-241.4, 506.11) * mm, "mid": v(-244.3, 497.98) * mm, "end": v(-246.93, 489.75) * mm});
            skLineSegment(sketch, "E41.19.6", {"start": v(-268.96, 528.02) * mm, "end": v(-241.4, 506.11) * mm});
            skArc(sketch, "E41.19.7", {"start": v(-288.66, 455.73) * mm, "mid": v(-287.61, 462.84) * mm, "end": v(-286.38, 469.9) * mm});
            skArc(sketch, "E41.19.8", {"start": v(-308.75, 458.45) * mm, "mid": v(-304.61, 482.05) * mm, "end": v(-298.64, 505.25) * mm});
            skArc(sketch, "E41.19.9", {"start": v(-251.31, 473.04) * mm, "mid": v(-249.26, 481.43) * mm, "end": v(-246.93, 489.75) * mm});
            skArc(sketch, "E41.19.10", {"start": v(-281.33, 549.9) * mm, "mid": v(-290.86, 527.91) * mm, "end": v(-298.64, 505.25) * mm});
            skLineSegment(sketch, "E41.19.11", {"start": v(-308.75, 458.45) * mm, "end": v(-288.66, 455.73) * mm});
            skArc(sketch, "E41.19.12", {"start": v(-263.06, 541.1) * mm, "mid": v(-266.1, 534.6) * mm, "end": v(-268.96, 528.02) * mm});
            skLineSegment(sketch, "E41.19.13", {"start": v(-281.33, 549.9) * mm, "end": v(-263.06, 541.1) * mm});
            skSolve(sketch);
        }
        {
            var Q0;
            Q0=makeQuery(id+"F6.imprint","IMPRINT",FACE,{"disambiguationData":[TD([[makeQuery(id+"F6.imprint","IMPRINT",EDGE,{"derivedFrom":sQuery(id+"F6.wireOp",EDGE,"E30")}),-1.0]])]});
            var Q1;
            Q1=makeQuery(id+"F6.imprint","IMPRINT",FACE,{"disambiguationData":[TD([[makeQuery(id+"F6.imprint","IMPRINT",EDGE,{"derivedFrom":sQuery(id+"F6.wireOp",EDGE,"E41.19.2")}),1.0]])]});
            var Q2;
            Q2=makeQuery(id+"F6.imprint","IMPRINT",FACE,{"disambiguationData":[TD([[makeQuery(id+"F6.imprint","IMPRINT",EDGE,{"derivedFrom":sQuery(id+"F6.wireOp",EDGE,"E41.18.2")}),1.0]])]});
            var Q3;
            Q3=makeQuery(id+"F6.imprint","IMPRINT",FACE,{"disambiguationData":[TD([[makeQuery(id+"F6.imprint","IMPRINT",EDGE,{"derivedFrom":sQuery(id+"F6.wireOp",EDGE,"E41.17.2")}),1.0]])]});
            var Q4;
            Q4=makeQuery(id+"F6.imprint","IMPRINT",FACE,{"disambiguationData":[TD([[makeQuery(id+"F6.imprint","IMPRINT",EDGE,{"derivedFrom":sQuery(id+"F6.wireOp",EDGE,"E41.16.2")}),1.0]])]});
            var Q5;
            Q5=makeQuery(id+"F6.imprint","IMPRINT",FACE,{"disambiguationData":[TD([[makeQuery(id+"F6.imprint","IMPRINT",EDGE,{"derivedFrom":sQuery(id+"F6.wireOp",EDGE,"E41.15.2")}),1.0]])]});
            var Q6;
            Q6=makeQuery(id+"F6.imprint","IMPRINT",FACE,{"disambiguationData":[TD([[makeQuery(id+"F6.imprint","IMPRINT",EDGE,{"derivedFrom":sQuery(id+"F6.wireOp",EDGE,"E41.14.2")}),1.0]])]});
            var Q7;
            Q7=makeQuery(id+"F6.imprint","IMPRINT",FACE,{"disambiguationData":[TD([[makeQuery(id+"F6.imprint","IMPRINT",EDGE,{"derivedFrom":sQuery(id+"F6.wireOp",EDGE,"E41.13.2")}),1.0]])]});
            var Q8;
            Q8=makeQuery(id+"F6.imprint","IMPRINT",FACE,{"disambiguationData":[TD([[makeQuery(id+"F6.imprint","IMPRINT",EDGE,{"derivedFrom":sQuery(id+"F6.wireOp",EDGE,"E41.12.2")}),1.0]])]});
            var Q9;
            Q9=makeQuery(id+"F6.imprint","IMPRINT",FACE,{"disambiguationData":[TD([[makeQuery(id+"F6.imprint","IMPRINT",EDGE,{"derivedFrom":sQuery(id+"F6.wireOp",EDGE,"E41.11.2")}),1.0]])]});
            var Q10;
            Q10=makeQuery(id+"F6.imprint","IMPRINT",FACE,{"disambiguationData":[TD([[makeQuery(id+"F6.imprint","IMPRINT",EDGE,{"derivedFrom":sQuery(id+"F6.wireOp",EDGE,"E41.10.2")}),1.0]])]});
            var Q11;
            Q11=makeQuery(id+"F6.imprint","IMPRINT",FACE,{"disambiguationData":[TD([[makeQuery(id+"F6.imprint","IMPRINT",EDGE,{"derivedFrom":sQuery(id+"F6.wireOp",EDGE,"E41.9.2")}),1.0]])]});
            var Q12;
            Q12=makeQuery(id+"F6.imprint","IMPRINT",FACE,{"disambiguationData":[TD([[makeQuery(id+"F6.imprint","IMPRINT",EDGE,{"derivedFrom":sQuery(id+"F6.wireOp",EDGE,"E41.8.2")}),1.0]])]});
            var Q13;
            Q13=makeQuery(id+"F6.imprint","IMPRINT",FACE,{"disambiguationData":[TD([[makeQuery(id+"F6.imprint","IMPRINT",EDGE,{"derivedFrom":sQuery(id+"F6.wireOp",EDGE,"E41.7.2")}),1.0]])]});
            var Q14;
            Q14=makeQuery(id+"F6.imprint","IMPRINT",FACE,{"disambiguationData":[TD([[makeQuery(id+"F6.imprint","IMPRINT",EDGE,{"derivedFrom":sQuery(id+"F6.wireOp",EDGE,"E41.6.2")}),1.0]])]});
            var Q15;
            Q15=makeQuery(id+"F6.imprint","IMPRINT",FACE,{"disambiguationData":[TD([[makeQuery(id+"F6.imprint","IMPRINT",EDGE,{"derivedFrom":sQuery(id+"F6.wireOp",EDGE,"E41.5.2")}),1.0]])]});
            var Q16;
            Q16=makeQuery(id+"F6.imprint","IMPRINT",FACE,{"disambiguationData":[TD([[makeQuery(id+"F6.imprint","IMPRINT",EDGE,{"derivedFrom":sQuery(id+"F6.wireOp",EDGE,"E41.4.2")}),1.0]])]});
            var Q17;
            Q17=makeQuery(id+"F6.imprint","IMPRINT",FACE,{"disambiguationData":[TD([[makeQuery(id+"F6.imprint","IMPRINT",EDGE,{"derivedFrom":sQuery(id+"F6.wireOp",EDGE,"E41.3.2")}),1.0]])]});
            var Q18;
            Q18=makeQuery(id+"F6.imprint","IMPRINT",FACE,{"disambiguationData":[TD([[makeQuery(id+"F6.imprint","IMPRINT",EDGE,{"derivedFrom":sQuery(id+"F6.wireOp",EDGE,"E41.2.2")}),1.0]])]});
            var Q19;
            Q19=makeQuery(id+"F6.imprint","IMPRINT",FACE,{"disambiguationData":[TD([[makeQuery(id+"F6.imprint","IMPRINT",EDGE,{"derivedFrom":sQuery(id+"F6.wireOp",EDGE,"E41.1.2")}),1.0]])]});
            extrude(context, id + "F7", {"entities" : qUnion([Q0, Q1, Q2, Q3, Q4, Q5, Q6, Q7, Q8, Q9, Q10, Q11, Q12, Q13, Q14, Q15, Q16, Q17, Q18, Q19]), "depth" : 25.4 * mm, "offsetDistance" : 25.4 * mm});
        }
        {
            var Q0;
            Q0=makeQuery(id+"F3.opExtrude","CAP_FACE",FACE,{"disambiguationData":[OSD([sQuery(id+"F2.wireOp",EDGE,"E25")])],"isStart":false});
            var sketch = newSketch(context, id + "F8", { "sketchPlane" : qUnion([Q0])});
            skCircle(sketch, "E42.0", {"center": v(-6.35, 417.61) * mm, "radius": 400.05 * mm});
            skFitSpline(sketch, "E43", {"points": [v(-13.74, 409.14) * mm, v(-66.89, 382.83) * mm, v(-105.55, 366.72) * mm, v(-144.74, 355.45) * mm, v(-180.71, 348.47) * mm, v(-237.09, 342.56) * mm, v(-237.63, 341.49) * mm, v(-231.3, 331.19) * mm, v(-173.86, 292.1) * mm, v(-141.87, 277.02) * mm, v(-116.75, 273.2) * mm, v(-93.15, 274.84) * mm, v(-81.7, 283.74) * mm, v(-67.52, 302.47) * mm, v(-11.36, 407.23) * mm, v(-13.74, 409.14) * mm]});
            skSolve(sketch);
        }
        {
            var Q0;
            Q0=makeQuery(id+"F8.imprint","IMPRINT",FACE,{"disambiguationData":[TD([[makeQuery(id+"F8.imprint","IMPRINT",EDGE,{"derivedFrom":sQuery(id+"F8.wireOp",EDGE,"E43")}),1.0]])]});
            extrude(context, id + "F9", {"entities" : qUnion([Q0]), "depth" : 50.8 * mm, "offsetDistance" : 25.4 * mm});
        }
    });
